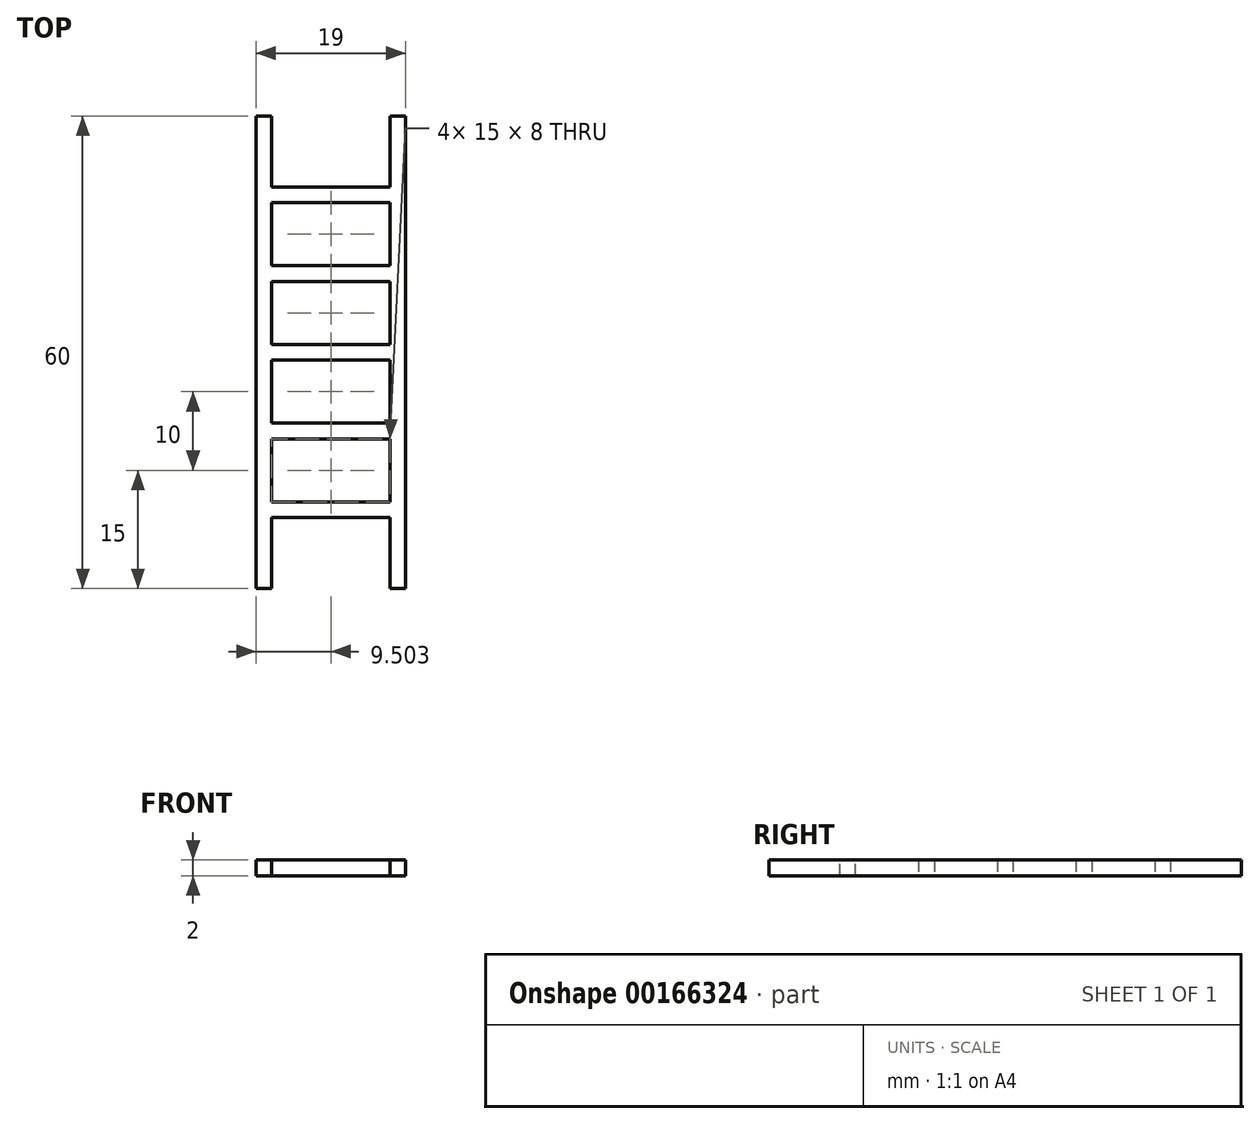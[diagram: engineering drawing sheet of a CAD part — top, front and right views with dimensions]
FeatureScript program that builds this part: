
annotation { "Feature Type Name" : "Feature", "Feature Type Description" : "" }
export const myFeature = defineFeature(function(context is Context, id is Id, definition is map)
    precondition{}
    {
        {
            var Q0;
            Q0=qCreatedBy(makeId("Front.planeOp"),FACE);
            var sketch = newSketch(context, id + "F0", { "sketchPlane" : qUnion([Q0])});
            skLineSegment(sketch, "E0.bottom", {"start": v(-30.22, 16.27) * mm, "end": v(-28.22, 16.27) * mm});
            skLineSegment(sketch, "E0.top", {"start": v(-30.22, 14.27) * mm, "end": v(-28.22, 14.27) * mm});
            skLineSegment(sketch, "E0.left", {"start": v(-30.22, 16.27) * mm, "end": v(-30.22, 14.27) * mm});
            skLineSegment(sketch, "E0.right", {"start": v(-28.22, 16.27) * mm, "end": v(-28.22, 14.27) * mm});
            skLineSegment(sketch, "E1.bottom", {"start": v(-13.22, 16.27) * mm, "end": v(-11.22, 16.27) * mm});
            skLineSegment(sketch, "E1.top", {"start": v(-13.22, 14.27) * mm, "end": v(-11.22, 14.27) * mm});
            skLineSegment(sketch, "E1.left", {"start": v(-13.22, 16.27) * mm, "end": v(-13.22, 14.27) * mm});
            skLineSegment(sketch, "E1.right", {"start": v(-11.22, 16.27) * mm, "end": v(-11.22, 14.27) * mm});
            skPoint(sketch, "E1.middle", {"position": v(-12.22, 15.27) * mm});
            skPoint(sketch, "E1.middle.positionSnap0", {"position": v(-28.22, 15.27) * mm});
            skPoint(sketch, "E1.centerSnap0", {"position": v(-28.22, 15.27) * mm});
            skSolve(sketch);
        }
        {
            var Q0;
            Q0 = qSketchRegion(id + "F0", true);
            extrude(context, id + "F1", {"entities" : qUnion([Q0]), "depth" : 60 * mm});
        }
        {
            var Q0;
            Q0=makeQuery(id+"F1.opExtrude","SWEPT_FACE",FACE,{"disambiguationData":[OSD([sQuery(id+"F0.wireOp",EDGE,"E0.right")])]});
            var sketch = newSketch(context, id + "F2", { "sketchPlane" : qUnion([Q0])});
            skLineSegment(sketch, "E2.bottom", {"start": v(-49, 14.27) * mm, "end": v(-51, 14.27) * mm});
            skLineSegment(sketch, "E2.top", {"start": v(-49, 16.27) * mm, "end": v(-51, 16.27) * mm});
            skLineSegment(sketch, "E2.left", {"start": v(-49, 14.27) * mm, "end": v(-49, 16.27) * mm});
            skLineSegment(sketch, "E2.right", {"start": v(-51, 14.27) * mm, "end": v(-51, 16.27) * mm});
            skPoint(sketch, "E2.middle", {"position": v(-50, 15.27) * mm});
            skPoint(sketch, "E2.middle.positionSnap0", {"position": v(-60, 15.27) * mm});
            skPoint(sketch, "E2.centerSnap0", {"position": v(-60, 15.27) * mm});
            skLineSegment(sketch, "E3.bottom", {"start": v(-41, 16.27) * mm, "end": v(-39, 16.27) * mm});
            skLineSegment(sketch, "E3.top", {"start": v(-41, 14.27) * mm, "end": v(-39, 14.27) * mm});
            skLineSegment(sketch, "E3.left", {"start": v(-41, 16.27) * mm, "end": v(-41, 14.27) * mm});
            skLineSegment(sketch, "E3.right", {"start": v(-39, 16.27) * mm, "end": v(-39, 14.27) * mm});
            skPoint(sketch, "E3.middle", {"position": v(-40, 15.27) * mm});
            skPoint(sketch, "E3.middle.positionSnap0", {"position": v(-49, 15.27) * mm});
            skPoint(sketch, "E3.centerSnap0", {"position": v(-49, 15.27) * mm});
            skLineSegment(sketch, "E4.bottom", {"start": v(-31, 16.27) * mm, "end": v(-29, 16.27) * mm});
            skLineSegment(sketch, "E4.top", {"start": v(-31, 14.27) * mm, "end": v(-29, 14.27) * mm});
            skLineSegment(sketch, "E4.left", {"start": v(-31, 16.27) * mm, "end": v(-31, 14.27) * mm});
            skLineSegment(sketch, "E4.right", {"start": v(-29, 16.27) * mm, "end": v(-29, 14.27) * mm});
            skPoint(sketch, "E4.middle", {"position": v(-30, 15.27) * mm});
            skLineSegment(sketch, "E5.bottom", {"start": v(-21, 16.27) * mm, "end": v(-19, 16.27) * mm});
            skLineSegment(sketch, "E5.top", {"start": v(-21, 14.27) * mm, "end": v(-19, 14.27) * mm});
            skLineSegment(sketch, "E5.left", {"start": v(-21, 16.27) * mm, "end": v(-21, 14.27) * mm});
            skLineSegment(sketch, "E5.right", {"start": v(-19, 16.27) * mm, "end": v(-19, 14.27) * mm});
            skPoint(sketch, "E5.middle", {"position": v(-20, 15.27) * mm});
            skLineSegment(sketch, "E6.bottom", {"start": v(-11, 16.27) * mm, "end": v(-9, 16.27) * mm});
            skLineSegment(sketch, "E6.top", {"start": v(-11, 14.27) * mm, "end": v(-9, 14.27) * mm});
            skLineSegment(sketch, "E6.left", {"start": v(-11, 16.27) * mm, "end": v(-11, 14.27) * mm});
            skLineSegment(sketch, "E6.right", {"start": v(-9, 16.27) * mm, "end": v(-9, 14.27) * mm});
            skPoint(sketch, "E6.middle", {"position": v(-10, 15.27) * mm});
            skSolve(sketch);
        }
        {
            var Q0;
            Q0 = qSketchRegion(id + "F2", true);
            extrude(context, id + "F3", {"entities" : qUnion([Q0]), "operationType" : NewBodyOperationType.ADD, "depth" : 15 * mm});
        }
    });
